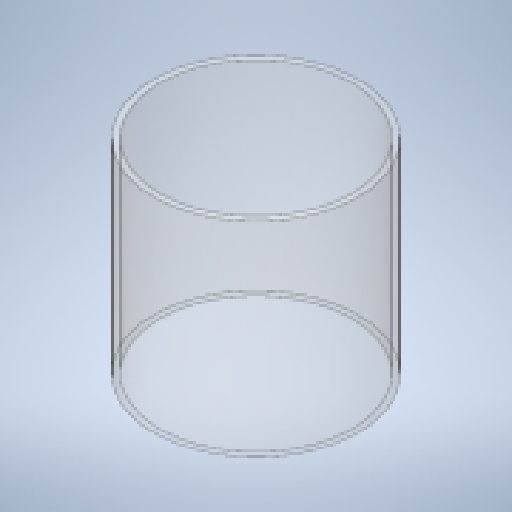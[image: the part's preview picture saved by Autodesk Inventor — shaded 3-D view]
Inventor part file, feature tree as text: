
AUTODESK INVENTOR PART (.ipt)
format: ipt  version: 2024.3 (Build 283343000, 343)  size: 144,896 bytes
history: native  units: mm
features: other x1, extrude x1, sketch x1
ambient origin geometry x8: Origin, YZ Plane, XZ Plane, XY Plane, X Axis, Y Axis, Z Axis, Center Point
bodies: Body1 (feature_tree)
feature tree (3):
  other  "Sólido1"
  extrude  "Extrusión1"  [1 undecoded]
  sketch  "Boceto1"  dims[d3=0.0mm]
note: 1 required parameter value undecoded (feature->parameter linkage not recoverable at this tier; creation-order binding heuristic only, values carry confidence <= 0.55)
